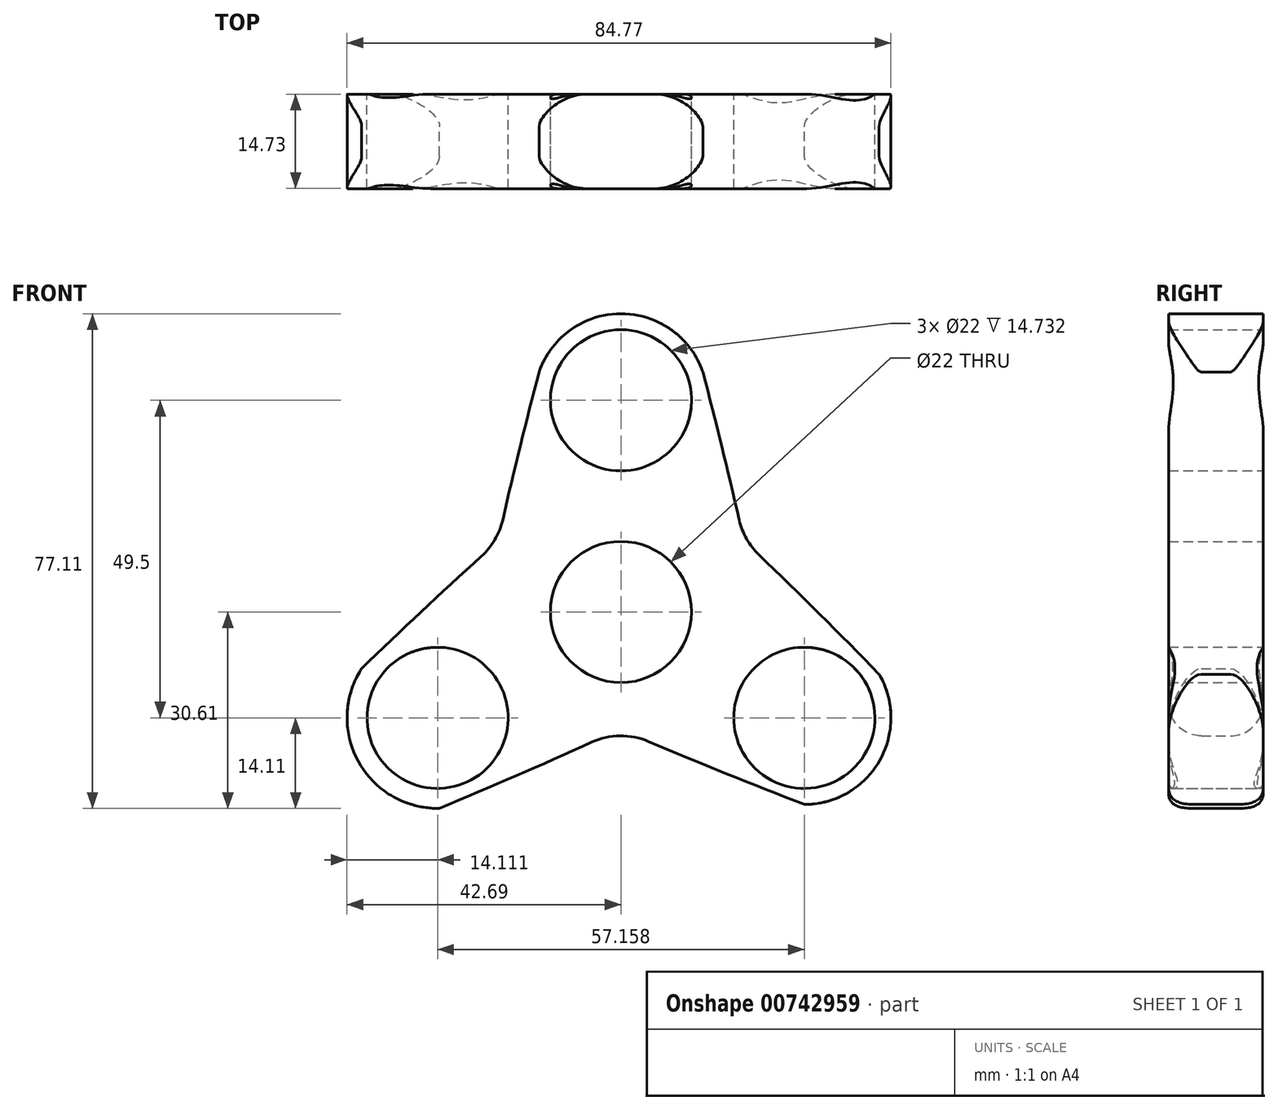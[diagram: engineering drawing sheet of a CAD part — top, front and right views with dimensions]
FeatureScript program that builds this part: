
annotation { "Feature Type Name" : "Feature", "Feature Type Description" : "" }
export const myFeature = defineFeature(function(context is Context, id is Id, definition is map)
    precondition{}
    {
        {
            var Q0;
            Q0=qCreatedBy(makeId("Front.planeOp"),FACE);
            var sketch = newSketch(context, id + "F0", { "sketchPlane" : qUnion([Q0])});
            skCircle(sketch, "E0", {"center": v(0, 0) * mm, "radius": 11 * mm});
            skLineSegment(sketch, "E1", {"start": v(0, 0) * mm, "end": v(0, 33) * mm});
            skLineSegment(sketch, "E2", {"start": v(0, 33) * mm, "end": v(0, 0) * mm});
            skLineSegment(sketch, "E3", {"start": v(0, 0) * mm, "end": v(28.58, -16.5) * mm});
            skLineSegment(sketch, "E4", {"start": v(0, 0) * mm, "end": v(-28.58, -16.5) * mm});
            skCircle(sketch, "E5", {"center": v(-28.58, -16.5) * mm, "radius": 11 * mm});
            skCircle(sketch, "E6", {"center": v(28.58, -16.5) * mm, "radius": 11 * mm});
            skCircle(sketch, "E7", {"center": v(0, 33) * mm, "radius": 11 * mm});
            skCircle(sketch, "E8", {"center": v(0, 33) * mm, "radius": 13.5 * mm});
            skCircle(sketch, "E9", {"center": v(28.58, -16.5) * mm, "radius": 13.5 * mm});
            skCircle(sketch, "E10", {"center": v(-28.58, -16.5) * mm, "radius": 14.1 * mm});
            skLineSegment(sketch, "E11", {"start": v(12.77, 37.39) * mm, "end": v(20.67, 23.84) * mm});
            skLineSegment(sketch, "E12", {"start": v(-12.77, 37.39) * mm, "end": v(-20.79, 23.98) * mm});
            skLineSegment(sketch, "E13", {"start": v(-28.58, -30.6) * mm, "end": v(-11, -30.42) * mm});
            skLineSegment(sketch, "E14", {"start": v(-28.58, -16.5) * mm, "end": v(29.15, 16.83) * mm});
            skLineSegment(sketch, "E15", {"start": v(28.58, -16.5) * mm, "end": v(-29.14, 16.82) * mm});
            skArc(sketch, "E16", {"start": v(-31.5, 6.08) * mm, "mid": v(-19.7, 11.18) * mm, "end": v(-20.79, 23.98) * mm});
            skArc(sketch, "E17", {"start": v(11, -30.19) * mm, "mid": v(-0.12, -19.3) * mm, "end": v(-11, -30.42) * mm});
            skArc(sketch, "E18", {"start": v(20.67, 23.84) * mm, "mid": v(19.65, 11.29) * mm, "end": v(31.08, 6) * mm});
            skLineSegment(sketch, "E19.trimOffspring", {"start": v(-31.5, 6.08) * mm, "end": v(-40.94, -9.7) * mm});
            skLineSegment(sketch, "E20.trimOffspring", {"start": v(31.08, 6) * mm, "end": v(40.24, -9.7) * mm});
            skLineSegment(sketch, "E21.trimOffspring", {"start": v(11, -30.19) * mm, "end": v(28.58, -30) * mm});
            skSolve(sketch);
        }
        {
            var Q0;
            Q0 = qSketchRegion(id + "F0", true);
            extrude(context, id + "F1", {"entities" : qUnion([Q0]), "depth" : 14.73 * mm, "offsetDistance" : 25.4 * mm});
        }
        {
            var Q0;
            Q0=makeQuery(id+"F1.opExtrude","SWEPT_EDGE",EDGE,{"disambiguationData":[OSD([sQuery(id+"F0.wireOp",EDGE,"E11"),sQuery(id+"F0.wireOp",EDGE,"E18")])]});
            var Q1;
            Q1=makeQuery(id+"F1.opExtrude","SWEPT_EDGE",EDGE,{"disambiguationData":[OSD([sQuery(id+"F0.wireOp",EDGE,"E18"),sQuery(id+"F0.wireOp",EDGE,"E20.trimOffspring")])]});
            var Q2;
            Q2=makeQuery(id+"F1.opExtrude","SWEPT_EDGE",EDGE,{"disambiguationData":[OSD([sQuery(id+"F0.wireOp",EDGE,"E17"),sQuery(id+"F0.wireOp",EDGE,"E21.trimOffspring")])]});
            var Q3;
            Q3=makeQuery(id+"F1.opExtrude","SWEPT_EDGE",EDGE,{"disambiguationData":[OSD([sQuery(id+"F0.wireOp",EDGE,"E13"),sQuery(id+"F0.wireOp",EDGE,"E17")])]});
            var Q4;
            Q4=makeQuery(id+"F1.opExtrude","SWEPT_EDGE",EDGE,{"disambiguationData":[OSD([sQuery(id+"F0.wireOp",EDGE,"E12"),sQuery(id+"F0.wireOp",EDGE,"E16")])]});
            var Q5;
            Q5=makeQuery(id+"F1.opExtrude","SWEPT_EDGE",EDGE,{"disambiguationData":[OSD([sQuery(id+"F0.wireOp",EDGE,"E16"),sQuery(id+"F0.wireOp",EDGE,"E19.trimOffspring")])]});
            fillet(context, id + "F2", {"entities" : qUnion([Q0, Q1, Q2, Q3, Q4, Q5]), "radius" : 762 * mm, "tangentPropagation" : true, "allowEdgeOverflow" : false});
        }
        {
            var Q0;
            Q0=makeQuery(id+"F1.opExtrude","CAP_EDGE",EDGE,{"disambiguationData":[OSD([sQuery(id+"F0.wireOp",EDGE,"E17")])],"isStart":false});
            var Q1;
            Q1=makeQuery(id+"F1.opExtrude","CAP_EDGE",EDGE,{"disambiguationData":[OSD([sQuery(id+"F0.wireOp",EDGE,"E18")])],"isStart":false});
            var Q2;
            Q2=makeQuery(id+"F1.opExtrude","CAP_EDGE",EDGE,{"disambiguationData":[OSD([sQuery(id+"F0.wireOp",EDGE,"E16")])],"isStart":false});
            fillet(context, id + "F3", {"entities" : qUnion([Q0, Q1, Q2]), "radius" : 5.08 * mm, "tangentPropagation" : true, "allowEdgeOverflow" : false});
        }
        {
            var Q0;
            Q0=makeQuery(id+"F1.opExtrude","CAP_EDGE",EDGE,{"disambiguationData":[OSD([sQuery(id+"F0.wireOp",EDGE,"E16")])],"isStart":true});
            var Q1;
            Q1=makeQuery(id+"F1.opExtrude","CAP_EDGE",EDGE,{"disambiguationData":[OSD([sQuery(id+"F0.wireOp",EDGE,"E18")])],"isStart":true});
            var Q2;
            Q2=makeQuery(id+"F1.opExtrude","CAP_EDGE",EDGE,{"disambiguationData":[OSD([sQuery(id+"F0.wireOp",EDGE,"E17")])],"isStart":true});
            fillet(context, id + "F4", {"entities" : qUnion([Q0, Q1, Q2]), "radius" : 5.08 * mm, "tangentPropagation" : true, "allowEdgeOverflow" : false});
        }
    });
